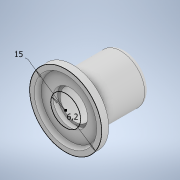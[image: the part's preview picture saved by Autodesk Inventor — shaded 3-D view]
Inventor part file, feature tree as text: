
AUTODESK INVENTOR PART (.ipt)
format: ipt  version: 2022.2 (Build 262287010, 287A)  size: 154,624 bytes
history: native  units: mm
features: sketch x2, revolve x1, fillet x1
ambient origin geometry x8: Origin, YZ Plane, XZ Plane, XY Plane, X Axis, Y Axis, Z Axis, Center Point
bodies: Body1 (feature_tree)
feature tree (4):
  sketch  "Skizze1"  dims[d1=15.0mm]
  revolve  "Umdrehung1"
  fillet  "Rundung2"  Radius=6.2mm
  sketch  "Skizze2"  dims[d7=11.5mm d8=1.0mm d10=1.5mm d11=3.1mm d12=7.5mm d13=1.0mm d14=90.0deg d15=1.0mm d16=3.6mm d17=2.0mm d18=5.0mm d19=1.0mm d20=6.5mm d21=0.45mm]
